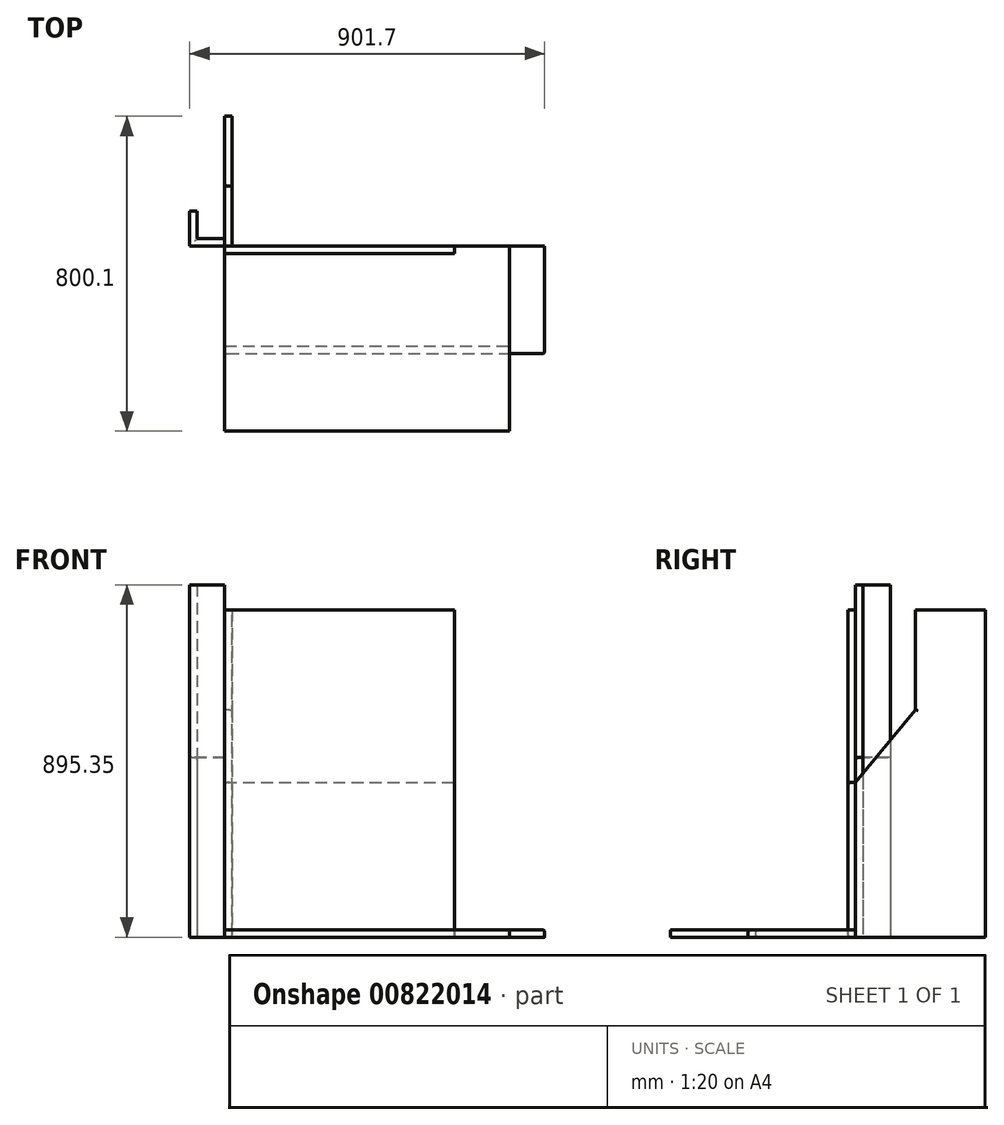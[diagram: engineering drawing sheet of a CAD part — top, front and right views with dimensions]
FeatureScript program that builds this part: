
annotation { "Feature Type Name" : "Feature", "Feature Type Description" : "" }
export const myFeature = defineFeature(function(context is Context, id is Id, definition is map)
    precondition{}
    {
        {
            var Q0;
            Q0=qCreatedBy(makeId("Top.planeOp"),FACE);
            var sketch = newSketch(context, id + "F0", { "sketchPlane" : qUnion([Q0])});
            skLineSegment(sketch, "E0.bottom", {"start": v(0, 0) * mm, "end": v(584.2, 0) * mm});
            skLineSegment(sketch, "E0.top", {"start": v(0, -19.05) * mm, "end": v(584.2, -19.05) * mm});
            skLineSegment(sketch, "E1", {"start": v(0, 0) * mm, "end": v(0, -19.05) * mm});
            skLineSegment(sketch, "E2", {"start": v(584.2, 0) * mm, "end": v(584.2, -19.05) * mm});
            skSolve(sketch);
        }
        {
            var Q0;
            Q0=makeQuery(id+"F0.imprint","IMPRINT",FACE,{"disambiguationData":[TD([[makeQuery(id+"F0.imprint","IMPRINT",EDGE,{"derivedFrom":sQuery(id+"F0.wireOp",EDGE,"E0.bottom")}),-1.0]])]});
            extrude(context, id + "F1", {"entities" : qUnion([Q0]), "depth" : 831.85 * mm, "offsetDistance" : 25.4 * mm});
        }
        {
            var Q0;
            Q0=qCreatedBy(makeId("Top.planeOp"),FACE);
            var sketch = newSketch(context, id + "F2", { "sketchPlane" : qUnion([Q0])});
            skLineSegment(sketch, "E3.bottom", {"start": v(0, 0) * mm, "end": v(723.9, 0) * mm});
            skLineSegment(sketch, "E3.top", {"start": v(0, -469.9) * mm, "end": v(723.9, -469.9) * mm});
            skLineSegment(sketch, "E3.left", {"start": v(0, 0) * mm, "end": v(0, -469.9) * mm});
            skLineSegment(sketch, "E3.right", {"start": v(723.9, 0) * mm, "end": v(723.9, -469.9) * mm});
            skSolve(sketch);
        }
        {
            var Q0;
            Q0=makeQuery(id+"F2.imprint","IMPRINT",FACE,{"disambiguationData":[TD([[makeQuery(id+"F2.imprint","IMPRINT",EDGE,{"derivedFrom":sQuery(id+"F2.wireOp",EDGE,"E3.bottom")}),-1.0]])]});
            extrude(context, id + "F3", {"entities" : qUnion([Q0]), "depth" : 19.05 * mm, "offsetDistance" : 25.4 * mm});
        }
        {
            var Q0;
            Q0=qCreatedBy(makeId("Top.planeOp"),FACE);
            var sketch = newSketch(context, id + "F4", { "sketchPlane" : qUnion([Q0])});
            skLineSegment(sketch, "E4.bottom", {"start": v(0, 0) * mm, "end": v(723.9, 0) * mm});
            skLineSegment(sketch, "E4.top", {"start": v(0, -254) * mm, "end": v(723.9, -254) * mm});
            skLineSegment(sketch, "E4.left", {"start": v(0, 0) * mm, "end": v(0, -254) * mm});
            skLineSegment(sketch, "E4.right", {"start": v(723.9, 0) * mm, "end": v(723.9, -254) * mm});
            skSolve(sketch);
        }
        {
            var Q0;
            Q0=makeQuery(id+"F4.imprint","IMPRINT",FACE,{"disambiguationData":[TD([[makeQuery(id+"F4.imprint","IMPRINT",EDGE,{"derivedFrom":sQuery(id+"F4.wireOp",EDGE,"E4.bottom")}),-1.0]])]});
            extrude(context, id + "F5", {"entities" : qUnion([Q0]), "depth" : 19.05 * mm, "offsetDistance" : 25.4 * mm});
        }
        {
            var Q0;
            Q0=qCreatedBy(makeId("Top.planeOp"),FACE);
            var sketch = newSketch(context, id + "F6", { "sketchPlane" : qUnion([Q0])});
            skLineSegment(sketch, "E5.bottom", {"start": v(0, 0) * mm, "end": v(812.8, 0) * mm});
            skLineSegment(sketch, "E5.top", {"start": v(0, -273.05) * mm, "end": v(812.8, -273.05) * mm});
            skLineSegment(sketch, "E5.left", {"start": v(0, 0) * mm, "end": v(0, -273.05) * mm});
            skLineSegment(sketch, "E5.right", {"start": v(812.8, 0) * mm, "end": v(812.8, -273.05) * mm});
            skSolve(sketch);
        }
        {
            var Q0;
            Q0=makeQuery(id+"F6.imprint","IMPRINT",FACE,{"disambiguationData":[TD([[makeQuery(id+"F6.imprint","IMPRINT",EDGE,{"derivedFrom":sQuery(id+"F6.wireOp",EDGE,"E5.bottom")}),-1.0]])]});
            extrude(context, id + "F7", {"entities" : qUnion([Q0]), "depth" : 19.05 * mm, "offsetDistance" : 25.4 * mm});
        }
        {
            var Q0;
            Q0=qCreatedBy(makeId("Top.planeOp"),FACE);
            var sketch = newSketch(context, id + "F8", { "sketchPlane" : qUnion([Q0])});
            skLineSegment(sketch, "E6", {"start": v(0, 0) * mm, "end": v(-88.9, 0) * mm});
            skLineSegment(sketch, "E7", {"start": v(-88.9, 0) * mm, "end": v(-88.9, 88.9) * mm});
            skLineSegment(sketch, "E8", {"start": v(-88.9, 88.9) * mm, "end": v(-69.85, 88.9) * mm});
            skLineSegment(sketch, "E9", {"start": v(-69.85, 88.9) * mm, "end": v(-69.85, 19.05) * mm});
            skLineSegment(sketch, "E10", {"start": v(-69.85, 19.05) * mm, "end": v(0, 19.05) * mm});
            skLineSegment(sketch, "E11", {"start": v(0, 19.05) * mm, "end": v(0, 0) * mm});
            skSolve(sketch);
        }
        {
            var Q0;
            Q0=makeQuery(id+"F8.imprint","IMPRINT",FACE,{"disambiguationData":[TD([[makeQuery(id+"F8.imprint","IMPRINT",EDGE,{"derivedFrom":sQuery(id+"F8.wireOp",EDGE,"E6")}),-1.0]])]});
            extrude(context, id + "F9", {"entities" : qUnion([Q0]), "depth" : 457.2 * mm, "offsetDistance" : 25.4 * mm});
        }
        {
            var Q0;
            Q0=qCreatedBy(makeId("Top.planeOp"),FACE);
            var sketch = newSketch(context, id + "F10", { "sketchPlane" : qUnion([Q0])});
            skLineSegment(sketch, "E12", {"start": v(0, 0) * mm, "end": v(-88.9, 0) * mm});
            skLineSegment(sketch, "E13", {"start": v(-88.9, 0) * mm, "end": v(-88.9, 19.05) * mm});
            skLineSegment(sketch, "E14", {"start": v(-69.85, 19.05) * mm, "end": v(0, 19.05) * mm});
            skLineSegment(sketch, "E15", {"start": v(0, 19.05) * mm, "end": v(0, 0) * mm});
            skLineSegment(sketch, "E16", {"start": v(-69.85, 19.05) * mm, "end": v(-69.85, 88.9) * mm});
            skLineSegment(sketch, "E17", {"start": v(-69.85, 88.9) * mm, "end": v(-88.9, 88.9) * mm});
            skLineSegment(sketch, "E18", {"start": v(-88.9, 88.9) * mm, "end": v(-88.9, 19.05) * mm});
            skSolve(sketch);
        }
        {
            var Q0;
            Q0=makeQuery(id+"F10.imprint","IMPRINT",FACE,{"disambiguationData":[TD([[makeQuery(id+"F10.imprint","IMPRINT",EDGE,{"derivedFrom":sQuery(id+"F10.wireOp",EDGE,"E12")}),-1.0]])]});
            extrude(context, id + "F11", {"entities" : qUnion([Q0]), "depth" : 895.35 * mm, "offsetDistance" : 25.4 * mm});
        }
        {
            var Q0;
            Q0=qCreatedBy(makeId("Right.planeOp"),FACE);
            var sketch = newSketch(context, id + "F12", { "sketchPlane" : qUnion([Q0])});
            skLineSegment(sketch, "E19", {"start": v(177.33, 421.17) * mm, "end": v(177.33, 295.45) * mm});
            skLineSegment(sketch, "E20", {"start": v(177.33, 295.45) * mm, "end": v(551.98, 670.1) * mm});
            skLineSegment(sketch, "E21", {"start": v(551.98, 670.1) * mm, "end": v(551.98, 795.82) * mm});
            skLineSegment(sketch, "E22", {"start": v(551.98, 795.82) * mm, "end": v(177.33, 421.17) * mm});
            skSolve(sketch);
        }
        {
            var Q0;
            Q0=qCreatedBy(makeId("Right.planeOp"),FACE);
            var sketch = newSketch(context, id + "F13", { "sketchPlane" : qUnion([Q0])});
            skLineSegment(sketch, "E23", {"start": v(0, 0) * mm, "end": v(330.2, 0) * mm});
            skLineSegment(sketch, "E24", {"start": v(330.2, 0) * mm, "end": v(330.2, 831.85) * mm});
            skLineSegment(sketch, "E25", {"start": v(152.4, 577.85) * mm, "end": v(0, 393.7) * mm});
            skLineSegment(sketch, "E26", {"start": v(0, 393.7) * mm, "end": v(0, 0) * mm});
            skLineSegment(sketch, "E27", {"start": v(362.6, 831.85) * mm, "end": v(330.2, 831.85) * mm});
            skLineSegment(sketch, "E28", {"start": v(362.6, 831.85) * mm, "end": v(152.4, 831.85) * mm});
            skLineSegment(sketch, "E29", {"start": v(152.4, 831.85) * mm, "end": v(152.4, 577.85) * mm});
            skSolve(sketch);
        }
        {
            var Q0;
            Q0=makeQuery(id+"F12.imprint","IMPRINT",FACE,{"disambiguationData":[TD([[makeQuery(id+"F12.imprint","IMPRINT",EDGE,{"derivedFrom":sQuery(id+"F12.wireOp",EDGE,"E19")}),1.0]])]});
            extrude(context, id + "F14", {"entities" : qUnion([Q0]), "depth" : 19.05 * mm, "offsetDistance" : 25.4 * mm});
        }
        {
            var Q0;
            Q0=makeQuery(id+"F13.imprint","IMPRINT",FACE,{"disambiguationData":[TD([[makeQuery(id+"F13.imprint","IMPRINT",EDGE,{"derivedFrom":sQuery(id+"F13.wireOp",EDGE,"E23")}),1.0]])]});
            extrude(context, id + "F15", {"entities" : qUnion([Q0]), "depth" : 19.05 * mm, "offsetDistance" : 25.4 * mm});
        }
        {
            var Q0;
            Q0=qCreatedBy(makeId("Front.planeOp"),FACE);
            var sketch = newSketch(context, id + "F16", { "sketchPlane" : qUnion([Q0])});
            skLineSegment(sketch, "E30.bottom", {"start": v(0, 0) * mm, "end": v(584.2, 0) * mm});
            skLineSegment(sketch, "E30.top", {"start": v(0, 393.7) * mm, "end": v(584.2, 393.7) * mm});
            skLineSegment(sketch, "E30.left", {"start": v(0, 0) * mm, "end": v(0, 393.7) * mm});
            skLineSegment(sketch, "E30.right", {"start": v(584.2, 0) * mm, "end": v(584.2, 393.7) * mm});
            skSolve(sketch);
        }
        {
            var Q0;
            Q0=makeQuery(id+"F16.imprint","IMPRINT",FACE,{"disambiguationData":[TD([[makeQuery(id+"F16.imprint","IMPRINT",EDGE,{"derivedFrom":sQuery(id+"F16.wireOp",EDGE,"E30.bottom")}),1.0]])]});
            extrude(context, id + "F17", {"entities" : qUnion([Q0]), "depth" : 19.05 * mm, "offsetDistance" : 25.4 * mm});
        }
        {
            var Q0;
            Q0=makeQuery(id+"F7.opExtrude","SWEPT_EDGE",EDGE,{"disambiguationData":[OSD([sQuery(id+"F6.wireOp",EDGE,"E5.top"),sQuery(id+"F6.wireOp",EDGE,"E5.left")])]});
            var Q1;
            Q1=makeQuery(id+"F7.opExtrude","SWEPT_EDGE",EDGE,{"disambiguationData":[OSD([sQuery(id+"F6.wireOp",EDGE,"E5.top"),sQuery(id+"F6.wireOp",EDGE,"E5.right")])]});
            var Q2;
            Q2=makeQuery(id+"F7.opExtrude","CAP_EDGE",EDGE,{"disambiguationData":[OSD([sQuery(id+"F6.wireOp",EDGE,"E5.right")])],"isStart":false});
            var Q3;
            Q3=makeQuery(id+"F7.opExtrude","CAP_EDGE",EDGE,{"disambiguationData":[OSD([sQuery(id+"F6.wireOp",EDGE,"E5.top")])],"isStart":false});
            var Q4;
            Q4=makeQuery(id+"F7.opExtrude","CAP_EDGE",EDGE,{"disambiguationData":[OSD([sQuery(id+"F6.wireOp",EDGE,"E5.left")])],"isStart":false});
            fillet(context, id + "F18", {"entities" : qUnion([Q0, Q1, Q2, Q3, Q4]), "radius" : 6.35 * mm, "tangentPropagation" : true, "allowEdgeOverflow" : false});
        }
        {
            var Q0;
            Q0=makeQuery(id+"F17.opExtrude","CAP_EDGE",EDGE,{"disambiguationData":[OSD([sQuery(id+"F16.wireOp",EDGE,"E30.top")])],"isStart":false});
            var Q1;
            Q1=makeQuery(id+"F17.opExtrude","CAP_EDGE",EDGE,{"disambiguationData":[OSD([sQuery(id+"F16.wireOp",EDGE,"E30.top")])],"isStart":true});
            var Q2;
            Q2=makeQuery(id+"F17.opExtrude","CAP_EDGE",EDGE,{"disambiguationData":[OSD([sQuery(id+"F16.wireOp",EDGE,"E30.bottom")])],"isStart":false});
            fillet(context, id + "F19", {"entities" : qUnion([Q0, Q1, Q2]), "radius" : 6.35 * mm, "tangentPropagation" : true, "allowEdgeOverflow" : false});
        }
        {
            var Q0;
            Q0=makeQuery(id+"F9.opExtrude","CAP_EDGE",EDGE,{"disambiguationData":[OSD([sQuery(id+"F8.wireOp",EDGE,"E6")])],"isStart":false});
            var Q1;
            Q1=makeQuery(id+"F9.opExtrude","CAP_EDGE",EDGE,{"disambiguationData":[OSD([sQuery(id+"F8.wireOp",EDGE,"E7")])],"isStart":false});
            var Q2;
            Q2=makeQuery(id+"F9.opExtrude","CAP_EDGE",EDGE,{"disambiguationData":[OSD([sQuery(id+"F8.wireOp",EDGE,"E9")])],"isStart":false});
            var Q3;
            Q3=makeQuery(id+"F9.opExtrude","CAP_EDGE",EDGE,{"disambiguationData":[OSD([sQuery(id+"F8.wireOp",EDGE,"E10")])],"isStart":false});
            fillet(context, id + "F20", {"entities" : qUnion([Q0, Q1, Q2, Q3]), "radius" : 6.35 * mm, "tangentPropagation" : true, "allowEdgeOverflow" : false});
        }
        {
            var Q0;
            Q0=makeQuery(id+"F15.opExtrude","CAP_EDGE",EDGE,{"disambiguationData":[OSD([sQuery(id+"F13.wireOp",EDGE,"E25")])],"isStart":false});
            var Q1;
            Q1=makeQuery(id+"F15.opExtrude","CAP_EDGE",EDGE,{"disambiguationData":[OSD([sQuery(id+"F13.wireOp",EDGE,"E25")])],"isStart":true});
            fillet(context, id + "F21", {"entities" : qUnion([Q0, Q1]), "radius" : 6.35 * mm, "tangentPropagation" : true, "allowEdgeOverflow" : false});
        }
        {
            var Q0;
            Q0=makeQuery(id+"F5.opExtrude","CAP_EDGE",EDGE,{"disambiguationData":[OSD([sQuery(id+"F4.wireOp",EDGE,"E4.top")])],"isStart":false});
            var Q1;
            Q1=makeQuery(id+"F5.opExtrude","CAP_EDGE",EDGE,{"disambiguationData":[OSD([sQuery(id+"F4.wireOp",EDGE,"E4.top")])],"isStart":true});
            fillet(context, id + "F22", {"entities" : qUnion([Q0, Q1]), "radius" : 6.35 * mm, "tangentPropagation" : true, "allowEdgeOverflow" : false});
        }
        {
            var Q0;
            Q0=makeQuery(id+"F15.opExtrude","CAP_EDGE",EDGE,{"disambiguationData":[OSD([sQuery(id+"F13.wireOp",EDGE,"E23")])],"isStart":false});
            var Q1;
            Q1=makeQuery(id+"F15.opExtrude","CAP_EDGE",EDGE,{"disambiguationData":[OSD([sQuery(id+"F13.wireOp",EDGE,"E23")])],"isStart":true});
            fillet(context, id + "F23", {"entities" : qUnion([Q0, Q1]), "radius" : 6.35 * mm, "tangentPropagation" : true, "allowEdgeOverflow" : false});
        }
        {
            var Q0;
            Q0=makeQuery(id+"F15.opExtrude","CAP_EDGE",EDGE,{"disambiguationData":[OSD([sQuery(id+"F13.wireOp",EDGE,"E29")])],"isStart":false});
            var Q1;
            Q1=makeQuery(id+"F15.opExtrude","CAP_EDGE",EDGE,{"disambiguationData":[OSD([sQuery(id+"F13.wireOp",EDGE,"E29")])],"isStart":true});
            fillet(context, id + "F24", {"entities" : qUnion([Q0, Q1]), "radius" : 6.35 * mm, "tangentPropagation" : true, "allowEdgeOverflow" : false});
        }
        {
            var Q0;
            Q0=makeQuery(id+"F9.opExtrude","SWEPT_EDGE",EDGE,{"disambiguationData":[OSD([sQuery(id+"F8.wireOp",EDGE,"E6"),sQuery(id+"F8.wireOp",EDGE,"E7")])]});
            var Q1;
            Q1=makeQuery(id+"F20.opFillet","BLEND_EDGE",EDGE,{"blendedFrom":[makeQuery(id+"F9.opExtrude","CAP_EDGE",EDGE,{"disambiguationData":[OSD([sQuery(id+"F8.wireOp",EDGE,"E6")])],"isStart":false}),makeQuery(id+"F9.opExtrude","CAP_EDGE",EDGE,{"disambiguationData":[OSD([sQuery(id+"F8.wireOp",EDGE,"E7")])],"isStart":false})],"blendedInto":[]});
            fillet(context, id + "F25", {"entities" : qUnion([Q0, Q1]), "radius" : 6.35 * mm, "tangentPropagation" : true, "allowEdgeOverflow" : false});
        }
        {
            var Q0;
            Q0=makeQuery(id+"F14.opExtrude","SWEPT_BODY",BODY,{"disambiguationData":[OSD([sQuery(id+"F12.wireOp",EDGE,"E19"),sQuery(id+"F12.wireOp",EDGE,"E20"),sQuery(id+"F12.wireOp",EDGE,"E21"),sQuery(id+"F12.wireOp",EDGE,"E22")])]});
            deleteBodies(context, id + "F26", {"entities" : qUnion([Q0])});
        }
    });
